# Revit family: Sanitary_Showers_hansgrohe_28417000-Raindance-Rainmaker-Overhead-sh_
name_source: partatom
category: Plumbing Fixtures
revit_build: Autodesk Revit 2015 (Build: 20140903_1530(x64)
units: mm (PartAtom-declared; Revit-internal decimal feet)

## types (1)
- Chrome 000
    BIMobject category = Showers
    BIMobject category code = sanitary-showers
    BIMobject main category = Sanitary
    BIMobject main category code = sanitary
    BOSUseNativeGeometries = 1
    Brand url = http://www.hansgrohe-int.com
    Default Elevation = 4' - 0"
    EAN code = https://4011097591742
    Edition number = 1
    IFC Classification = Sanitary Terminal
    Installation instructions = https://pro.hansgrohe-int.com
    Manufacturer country = Germany
    Manufacturer name = hansgrohe
    Masterformat 2014 Code = 22 41 23
    Masterformat 2014 Description = Residential Showers
    Material main = Chrome
    NBS Reference Code = 35-06-82
    NBS Reference Description = Shower Mixers
    OmniClass Code = 23-31 17 00
    OmniClass Description = Showers
    Product Guid = 7f28dbcb-30a6-4b5a-883f-9892f1dd0374
    Product SKU = 28417000
    Product data url = https://bimobject.com
    Product family = Raindance Rainmaker
    Product group = Overhead showers
    Product name = 28417000 Raindance Rainmaker Overhead shower 680/460 3jet without lighting 28417000
    Product url = https://pro.hansgrohe-int.com
    QR code = http://bimobject.com
    Technical description = https://pro.hansgrohe-int.com
    UNSPSC Code = 30181503
    Uniclass 1.4 Code = L7214
    Uniclass 1.4 Description = Showers
    Uniclass 2.0 Code = PR-35-06-82
    Uniclass 2.0 Description = Shower Mixers
    Uniclass 2015 Code = SL_35_80_80
    Uniclass 2015 Name = Showers
    Uniformat II Code = D2090
    Uniformat II Description = Other Plumbing Systems

## geometry (parser evidence)
native form markers: Sweep x3
no freeform markers — native parametric forms only
